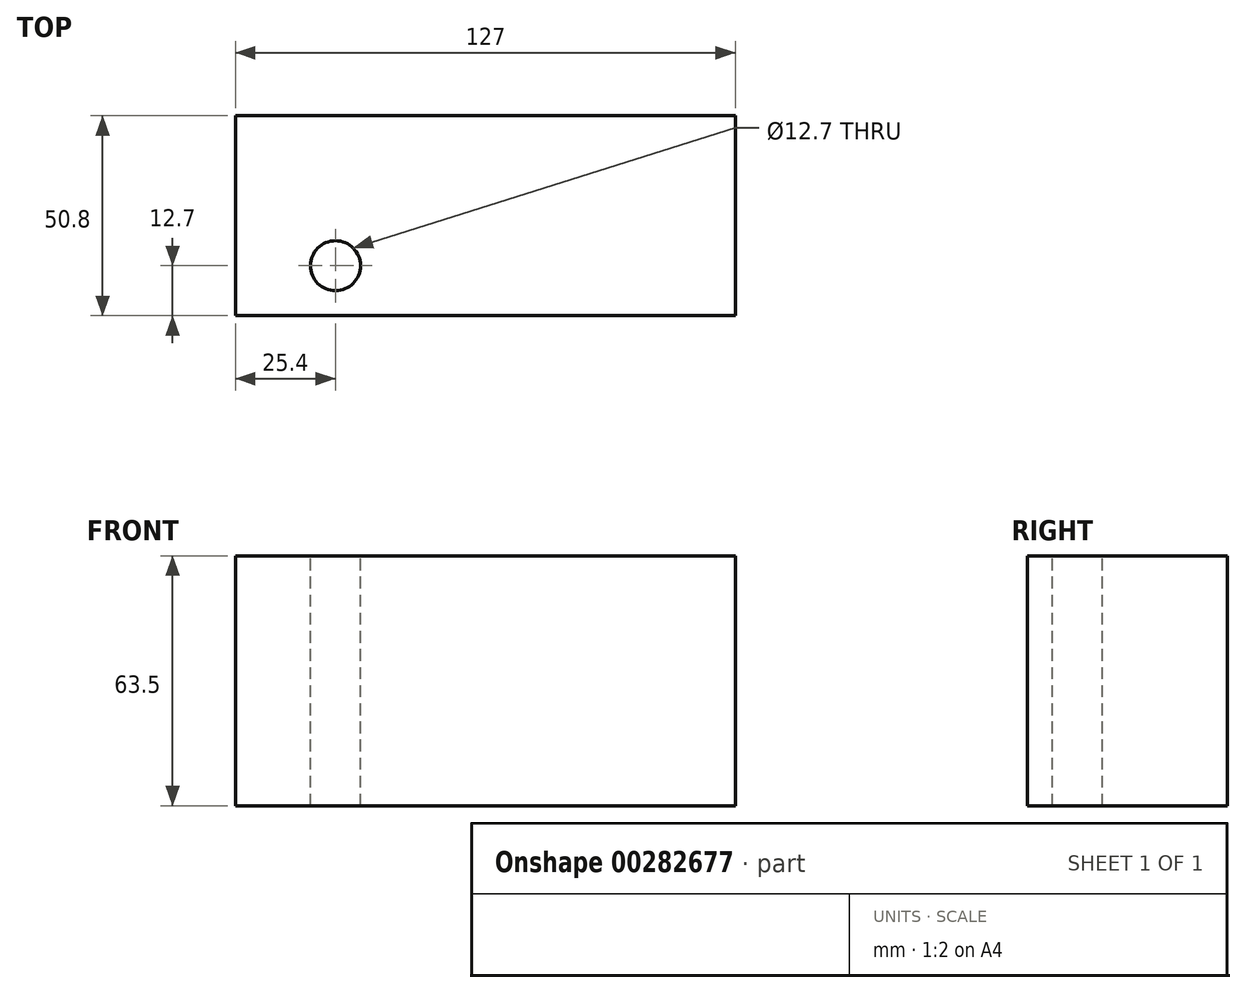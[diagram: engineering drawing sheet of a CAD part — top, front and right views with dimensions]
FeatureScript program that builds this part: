
annotation { "Feature Type Name" : "Feature", "Feature Type Description" : "" }
export const myFeature = defineFeature(function(context is Context, id is Id, definition is map)
    precondition{}
    {
        {
            var Q0;
            Q0=qCreatedBy(makeId("Front.planeOp"),FACE);
            var sketch = newSketch(context, id + "F0", { "sketchPlane" : qUnion([Q0])});
            skLineSegment(sketch, "E0.bottom", {"start": v(0, 0) * mm, "end": v(127, 0) * mm});
            skLineSegment(sketch, "E0.top", {"start": v(0, 63.5) * mm, "end": v(127, 63.5) * mm});
            skLineSegment(sketch, "E0.left", {"start": v(0, 0) * mm, "end": v(0, 63.5) * mm});
            skLineSegment(sketch, "E0.right", {"start": v(127, 0) * mm, "end": v(127, 63.5) * mm});
            skSolve(sketch);
        }
        {
            var Q0;
            Q0 = qSketchRegion(id + "F0", true);
            extrude(context, id + "F1", {"entities" : qUnion([Q0]), "oppositeDirection" : true, "depth" : 50.8 * mm});
        }
        {
            var Q0;
            Q0=makeQuery(id+"F1.opExtrude","SWEPT_FACE",FACE,{"disambiguationData":[OSD([sQuery(id+"F0.wireOp",EDGE,"E0.top")])]});
            var sketch = newSketch(context, id + "F2", { "sketchPlane" : qUnion([Q0])});
            skCircle(sketch, "E1", {"center": v(25.4, 12.7) * mm, "radius": 6.35 * mm});
            skSolve(sketch);
        }
        {
            var Q0;
            Q0 = qSketchRegion(id + "F2", true);
            extrude(context, id + "F3", {"entities" : qUnion([Q0]), "operationType" : NewBodyOperationType.REMOVE, "endBound" : BoundingType.THROUGH_ALL, "oppositeDirection" : true, "depth" : 139.95 * mm});
        }
    });
